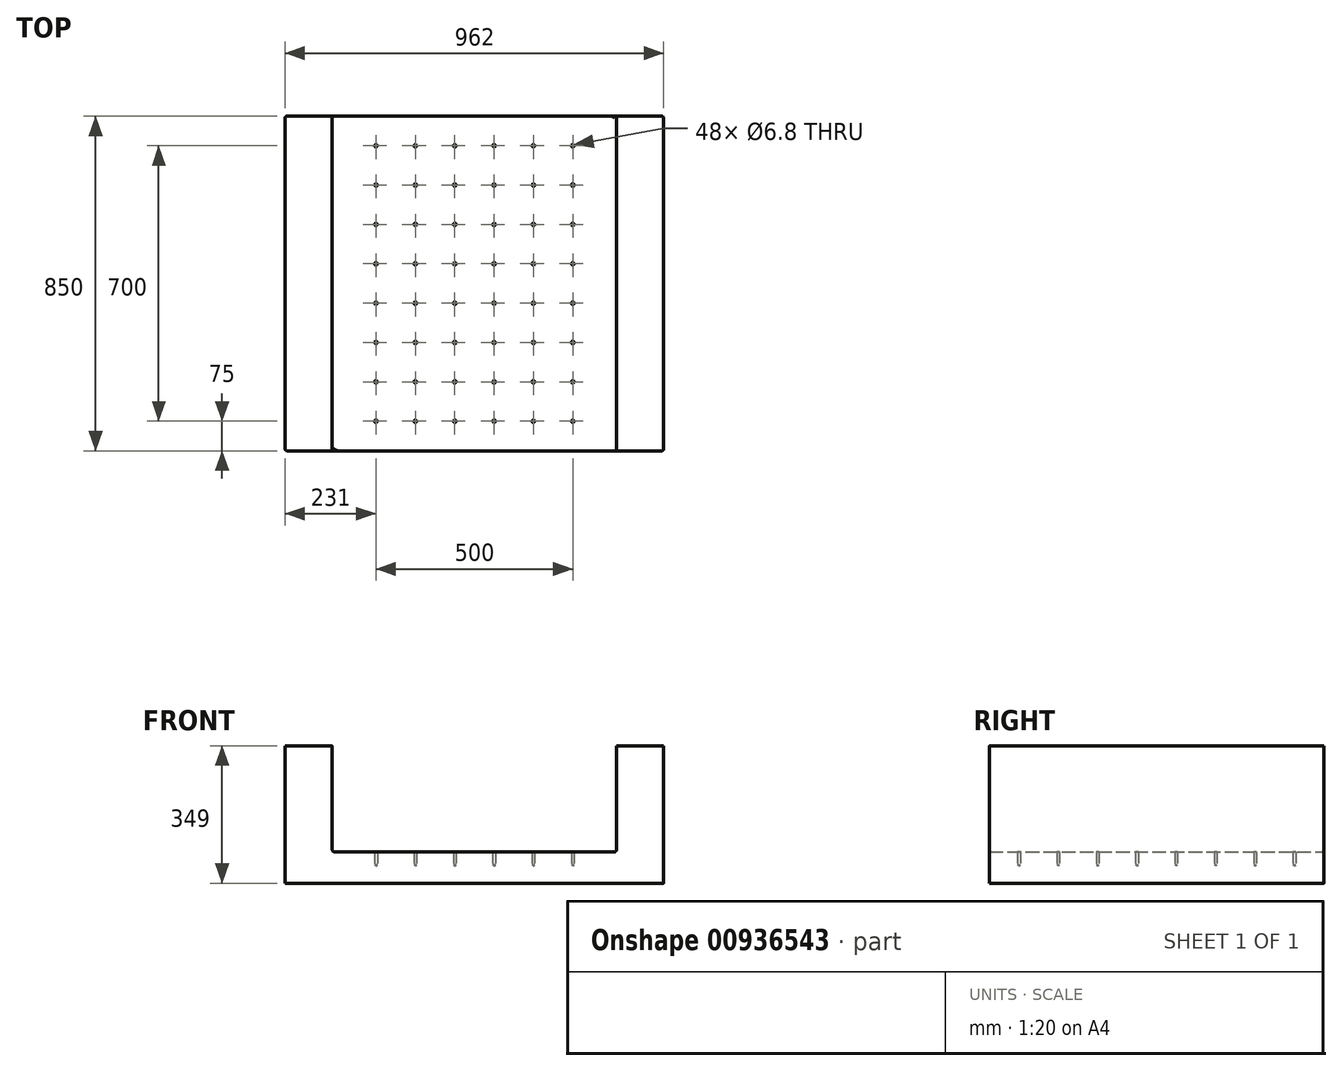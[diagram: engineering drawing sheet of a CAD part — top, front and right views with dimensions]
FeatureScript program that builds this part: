
annotation { "Feature Type Name" : "Feature", "Feature Type Description" : "" }
export const myFeature = defineFeature(function(context is Context, id is Id, definition is map)
    precondition{}
    {
        {
            var Q0;
            Q0=qCreatedBy(makeId("Front.planeOp"),FACE);
            var sketch = newSketch(context, id + "F0", { "sketchPlane" : qUnion([Q0])});
            skLineSegment(sketch, "E0", {"start": v(-361, 0) * mm, "end": v(0, 0) * mm});
            skLineSegment(sketch, "E1", {"start": v(-361, 0) * mm, "end": v(-361, 269) * mm});
            skLineSegment(sketch, "E2", {"start": v(-361, 269) * mm, "end": v(-481, 269) * mm});
            skLineSegment(sketch, "E3", {"start": v(-481, 269) * mm, "end": v(-481, -80) * mm});
            skLineSegment(sketch, "E4", {"start": v(-481, -80) * mm, "end": v(0, -80) * mm});
            skLineSegment(sketch, "E5.MirrorCS", {"start": v(361, 0) * mm, "end": v(0, 0) * mm});
            skLineSegment(sketch, "E6.MirrorCS", {"start": v(481, -80) * mm, "end": v(0, -80) * mm});
            skLineSegment(sketch, "E7.MirrorCS", {"start": v(361, 0) * mm, "end": v(361, 269) * mm});
            skLineSegment(sketch, "E8.MirrorCS", {"start": v(361, 269) * mm, "end": v(481, 269) * mm});
            skLineSegment(sketch, "E9.MirrorCS", {"start": v(481, 269) * mm, "end": v(481, -80) * mm});
            skSolve(sketch);
        }
        {
            var Q0;
            Q0=makeQuery(id+"F0.imprint","IMPRINT",FACE,{"disambiguationData":[TD([[makeQuery(id+"F0.imprint","IMPRINT",EDGE,{"derivedFrom":sQuery(id+"F0.wireOp",EDGE,"E0")}),-1.0]])]});
            extrude(context, id + "F1", {"entities" : qUnion([Q0]), "depth" : 850 * mm, "offsetDistance" : 25 * mm});
        }
        {
            var Q0;
            Q0=makeQuery(id+"F1.opExtrude","SWEPT_EDGE",EDGE,{"disambiguationData":[OSD([sQuery(id+"F0.wireOp",EDGE,"E0"),sQuery(id+"F0.wireOp",EDGE,"E1")])]});
            var Q1;
            Q1=makeQuery(id+"F1.opExtrude","SWEPT_EDGE",EDGE,{"disambiguationData":[OSD([sQuery(id+"F0.wireOp",EDGE,"E5.MirrorCS"),sQuery(id+"F0.wireOp",EDGE,"E7.MirrorCS")])]});
            var Q2;
            Q2=makeQuery(id+"F1.opExtrude","CAP_EDGE",EDGE,{"disambiguationData":[OSD([sQuery(id+"F0.wireOp",EDGE,"E1")])],"isStart":false});
            var Q3;
            Q3=makeQuery(id+"F1.opExtrude","CAP_EDGE",EDGE,{"disambiguationData":[OSD([sQuery(id+"F0.wireOp",EDGE,"E3")])],"isStart":false});
            var Q4;
            Q4=makeQuery(id+"F1.opExtrude","CAP_EDGE",EDGE,{"disambiguationData":[OSD([sQuery(id+"F0.wireOp",EDGE,"E9.MirrorCS")])],"isStart":false});
            var Q5;
            Q5=makeQuery(id+"F1.opExtrude","CAP_EDGE",EDGE,{"disambiguationData":[OSD([sQuery(id+"F0.wireOp",EDGE,"E9.MirrorCS")])],"isStart":true});
            var Q6;
            Q6=makeQuery(id+"F1.opExtrude","CAP_EDGE",EDGE,{"disambiguationData":[OSD([sQuery(id+"F0.wireOp",EDGE,"E7.MirrorCS")])],"isStart":true});
            var Q7;
            Q7=makeQuery(id+"F1.opExtrude","CAP_EDGE",EDGE,{"disambiguationData":[OSD([sQuery(id+"F0.wireOp",EDGE,"E3")])],"isStart":true});
            fillet(context, id + "F2", {"entities" : qUnion([Q0, Q1, Q2, Q3, Q4, Q5, Q6, Q7]), "radius" : 5 * mm, "tangentPropagation" : true, "allowEdgeOverflow" : false});
        }
        {
            var Q0;
            Q0=makeQuery(id+"F1.opExtrude","SWEPT_FACE",FACE,{"disambiguationData":[OSD([sQuery(id+"F0.wireOp",EDGE,"E0"),sQuery(id+"F0.wireOp",EDGE,"E5.MirrorCS")])]});
            var sketch = newSketch(context, id + "F3", { "sketchPlane" : qUnion([Q0])});
            skLineSegment(sketch, "E10", {"start": v(0, 0) * mm, "end": v(0, -845) * mm, "construction": true});
            skPoint(sketch, "E11", {"position": v(50, -775) * mm});
            skPoint(sketch, "E12.0.1.0", {"position": v(50, -675) * mm});
            skPoint(sketch, "E12.0.2.0", {"position": v(50, -575) * mm});
            skPoint(sketch, "E12.0.3.0", {"position": v(50, -475) * mm});
            skPoint(sketch, "E12.0.4.0", {"position": v(50, -375) * mm});
            skPoint(sketch, "E12.0.5.0", {"position": v(50, -275) * mm});
            skPoint(sketch, "E12.0.6.0", {"position": v(50, -175) * mm});
            skPoint(sketch, "E12.1.0.0", {"position": v(150, -775) * mm});
            skPoint(sketch, "E12.1.1.0", {"position": v(150, -675) * mm});
            skPoint(sketch, "E12.1.2.0", {"position": v(150, -575) * mm});
            skPoint(sketch, "E12.1.3.0", {"position": v(150, -475) * mm});
            skPoint(sketch, "E12.1.4.0", {"position": v(150, -375) * mm});
            skPoint(sketch, "E12.1.5.0", {"position": v(150, -275) * mm});
            skPoint(sketch, "E12.1.6.0", {"position": v(150, -175) * mm});
            skPoint(sketch, "E12.2.0.0", {"position": v(250, -775) * mm});
            skPoint(sketch, "E12.2.1.0", {"position": v(250, -675) * mm});
            skPoint(sketch, "E12.2.2.0", {"position": v(250, -575) * mm});
            skPoint(sketch, "E12.2.3.0", {"position": v(250, -475) * mm});
            skPoint(sketch, "E12.2.4.0", {"position": v(250, -375) * mm});
            skPoint(sketch, "E12.2.5.0", {"position": v(250, -275) * mm});
            skPoint(sketch, "E12.2.6.0", {"position": v(250, -175) * mm});
            skLineSegment(sketch, "E12.direction1", {"start": v(50, -775) * mm, "end": v(150, -775) * mm, "construction": true});
            skLineSegment(sketch, "E12.direction2", {"start": v(50, -775) * mm, "end": v(50, -675) * mm, "construction": true});
            skPoint(sketch, "E13.0.0.7", {"position": v(50, -75) * mm});
            skPoint(sketch, "E13.0.1.7", {"position": v(150, -75) * mm});
            skPoint(sketch, "E13.0.2.7", {"position": v(250, -75) * mm});
            skPoint(sketch, "E14.MirrorP", {"position": v(-50, -775) * mm});
            skPoint(sketch, "E15.MirrorP", {"position": v(-150, -175) * mm});
            skPoint(sketch, "E16.MirrorP", {"position": v(-150, -375) * mm});
            skPoint(sketch, "E17.MirrorP", {"position": v(-250, -675) * mm});
            skPoint(sketch, "E18.MirrorP", {"position": v(-150, -775) * mm});
            skPoint(sketch, "E19.MirrorP", {"position": v(-250, -775) * mm});
            skPoint(sketch, "E20.MirrorP", {"position": v(-50, -275) * mm});
            skLineSegment(sketch, "E21.MirrorCS", {"start": v(-50, -775) * mm, "end": v(-150, -775) * mm, "construction": true});
            skPoint(sketch, "E22.MirrorP", {"position": v(-50, -575) * mm});
            skPoint(sketch, "E23.MirrorP", {"position": v(-150, -75) * mm});
            skPoint(sketch, "E24.MirrorP", {"position": v(-50, -675) * mm});
            skPoint(sketch, "E25.MirrorP", {"position": v(-250, -75) * mm});
            skPoint(sketch, "E26.MirrorP", {"position": v(-150, -275) * mm});
            skPoint(sketch, "E27.MirrorP", {"position": v(-150, -675) * mm});
            skPoint(sketch, "E28.MirrorP", {"position": v(-50, -475) * mm});
            skPoint(sketch, "E29.MirrorP", {"position": v(-150, -475) * mm});
            skPoint(sketch, "E30.MirrorP", {"position": v(-250, -275) * mm});
            skPoint(sketch, "E31.MirrorP", {"position": v(-250, -575) * mm});
            skPoint(sketch, "E32.MirrorP", {"position": v(-50, -375) * mm});
            skLineSegment(sketch, "E33.MirrorCS", {"start": v(-50, -775) * mm, "end": v(-50, -675) * mm, "construction": true});
            skPoint(sketch, "E34.MirrorP", {"position": v(-50, -175) * mm});
            skPoint(sketch, "E35.MirrorP", {"position": v(-150, -575) * mm});
            skPoint(sketch, "E36.MirrorP", {"position": v(-250, -475) * mm});
            skPoint(sketch, "E37.MirrorP", {"position": v(-50, -75) * mm});
            skPoint(sketch, "E38.MirrorP", {"position": v(-250, -175) * mm});
            skPoint(sketch, "E39.MirrorP", {"position": v(-250, -375) * mm});
            skSolve(sketch);
        }
        {
            var Q0;
            Q0=sQuery(id+"F3.wireOp",VERTEX,"E12.direction2.end");
            var Q1;
            Q1=sQuery(id+"F3.wireOp",VERTEX,"E12.direction2.start");
            var Q2;
            Q2=sQuery(id+"F3.wireOp",VERTEX,"E23.MirrorP");
            var Q3;
            Q3=sQuery(id+"F3.wireOp",VERTEX,"E12.direction1.end");
            var Q4;
            Q4=sQuery(id+"F3.wireOp",VERTEX,"E13.0.2.7");
            var Q5;
            Q5=sQuery(id+"F3.wireOp",VERTEX,"E12.2.6.0");
            var Q6;
            Q6=sQuery(id+"F3.wireOp",VERTEX,"E33.MirrorCS.end");
            var Q7;
            Q7=sQuery(id+"F3.wireOp",VERTEX,"E27.MirrorP");
            var Q8;
            Q8=sQuery(id+"F3.wireOp",VERTEX,"E39.MirrorP");
            var Q9;
            Q9=sQuery(id+"F3.wireOp",VERTEX,"E21.MirrorCS.end");
            var Q10;
            Q10=sQuery(id+"F3.wireOp",VERTEX,"E12.0.2.0");
            var Q11;
            Q11=sQuery(id+"F3.wireOp",VERTEX,"E12.2.5.0");
            var Q12;
            Q12=sQuery(id+"F3.wireOp",VERTEX,"E13.0.0.7");
            var Q13;
            Q13=sQuery(id+"F3.wireOp",VERTEX,"E29.MirrorP");
            var Q14;
            Q14=sQuery(id+"F3.wireOp",VERTEX,"E28.MirrorP");
            var Q15;
            Q15=sQuery(id+"F3.wireOp",VERTEX,"E32.MirrorP");
            var Q16;
            Q16=sQuery(id+"F3.wireOp",VERTEX,"E30.MirrorP");
            var Q17;
            Q17=sQuery(id+"F3.wireOp",VERTEX,"E13.0.1.7");
            var Q18;
            Q18=sQuery(id+"F3.wireOp",VERTEX,"E26.MirrorP");
            var Q19;
            Q19=sQuery(id+"F3.wireOp",VERTEX,"E12.2.3.0");
            var Q20;
            Q20=sQuery(id+"F3.wireOp",VERTEX,"E33.MirrorCS.start");
            var Q21;
            Q21=sQuery(id+"F3.wireOp",VERTEX,"E25.MirrorP");
            var Q22;
            Q22=sQuery(id+"F3.wireOp",VERTEX,"E12.2.4.0");
            var Q23;
            Q23=sQuery(id+"F3.wireOp",VERTEX,"E15.MirrorP");
            var Q24;
            Q24=sQuery(id+"F3.wireOp",VERTEX,"E12.2.2.0");
            var Q25;
            Q25=sQuery(id+"F3.wireOp",VERTEX,"E12.0.3.0");
            var Q26;
            Q26=sQuery(id+"F3.wireOp",VERTEX,"E38.MirrorP");
            var Q27;
            Q27=sQuery(id+"F3.wireOp",VERTEX,"E31.MirrorP");
            var Q28;
            Q28=sQuery(id+"F3.wireOp",VERTEX,"E22.MirrorP");
            var Q29;
            Q29=sQuery(id+"F3.wireOp",VERTEX,"E12.2.1.0");
            var Q30;
            Q30=sQuery(id+"F3.wireOp",VERTEX,"E12.0.4.0");
            var Q31;
            Q31=sQuery(id+"F3.wireOp",VERTEX,"E37.MirrorP");
            var Q32;
            Q32=sQuery(id+"F3.wireOp",VERTEX,"E20.MirrorP");
            var Q33;
            Q33=sQuery(id+"F3.wireOp",VERTEX,"E16.MirrorP");
            var Q34;
            Q34=sQuery(id+"F3.wireOp",VERTEX,"E12.2.0.0");
            var Q35;
            Q35=sQuery(id+"F3.wireOp",VERTEX,"E12.0.5.0");
            var Q36;
            Q36=sQuery(id+"F3.wireOp",VERTEX,"E36.MirrorP");
            var Q37;
            Q37=sQuery(id+"F3.wireOp",VERTEX,"E19.MirrorP");
            var Q38;
            Q38=sQuery(id+"F3.wireOp",VERTEX,"E12.1.6.0");
            var Q39;
            Q39=sQuery(id+"F3.wireOp",VERTEX,"E12.0.6.0");
            var Q40;
            Q40=sQuery(id+"F3.wireOp",VERTEX,"E35.MirrorP");
            var Q41;
            Q41=sQuery(id+"F3.wireOp",VERTEX,"E12.1.5.0");
            var Q42;
            Q42=sQuery(id+"F3.wireOp",VERTEX,"E34.MirrorP");
            var Q43;
            Q43=sQuery(id+"F3.wireOp",VERTEX,"E17.MirrorP");
            var Q44;
            Q44=sQuery(id+"F3.wireOp",VERTEX,"E12.1.4.0");
            var Q45;
            Q45=sQuery(id+"F3.wireOp",VERTEX,"E12.1.3.0");
            var Q46;
            Q46=sQuery(id+"F3.wireOp",VERTEX,"E12.1.1.0");
            var Q47;
            Q47=sQuery(id+"F3.wireOp",VERTEX,"E12.1.2.0");
            var Q48;
            Q48=makeQuery(id+"F1.opExtrude","SWEPT_BODY",BODY,{"disambiguationData":[OSD([sQuery(id+"F0.wireOp",EDGE,"E0"),sQuery(id+"F0.wireOp",EDGE,"E1"),sQuery(id+"F0.wireOp",EDGE,"E2"),sQuery(id+"F0.wireOp",EDGE,"E3"),sQuery(id+"F0.wireOp",EDGE,"E4"),sQuery(id+"F0.wireOp",EDGE,"E5.MirrorCS"),sQuery(id+"F0.wireOp",EDGE,"E6.MirrorCS"),sQuery(id+"F0.wireOp",EDGE,"E7.MirrorCS"),sQuery(id+"F0.wireOp",EDGE,"E8.MirrorCS"),sQuery(id+"F0.wireOp",EDGE,"E9.MirrorCS")])]});
            hole(context, id + "F4", {"style" : HoleStyle.SIMPLE, "endStyle" : HoleEndStyle.BLIND, "standardTappedOrClearance" : lookupTablePath({ "standard" : "ISO", "engagement" : "75%", "pitch" : "1.25 mm", "size" : "M8", "type" : "Tapped" }), "standardBlindInLast" : lookupTablePath({ "standard" : "ISO", "fit" : "Normal", "engagement" : "75%", "pitch" : "1.25 mm", "size" : "M8", "type" : "Clearance & tapped" }), "holeDiameter" : 6.8 * mm, "majorDiameter" : 8 * mm, "showTappedDepth" : true, "holeDepth" : 33.75 * mm, "tappedDepth" : 30 * mm, "tapClearance" : 3, "locations" : qUnion([Q0, Q1, Q2, Q3, Q4, Q5, Q6, Q7, Q8, Q9, Q10, Q11, Q12, Q13, Q14, Q15, Q16, Q17, Q18, Q19, Q20, Q21, Q22, Q23, Q24, Q25, Q26, Q27, Q28, Q29, Q30, Q31, Q32, Q33, Q34, Q35, Q36, Q37, Q38, Q39, Q40, Q41, Q42, Q43, Q44, Q45, Q46, Q47]), "scope" : qUnion([Q48]), "startStyle" : HoleStartStyle.PART});
        }
    });
